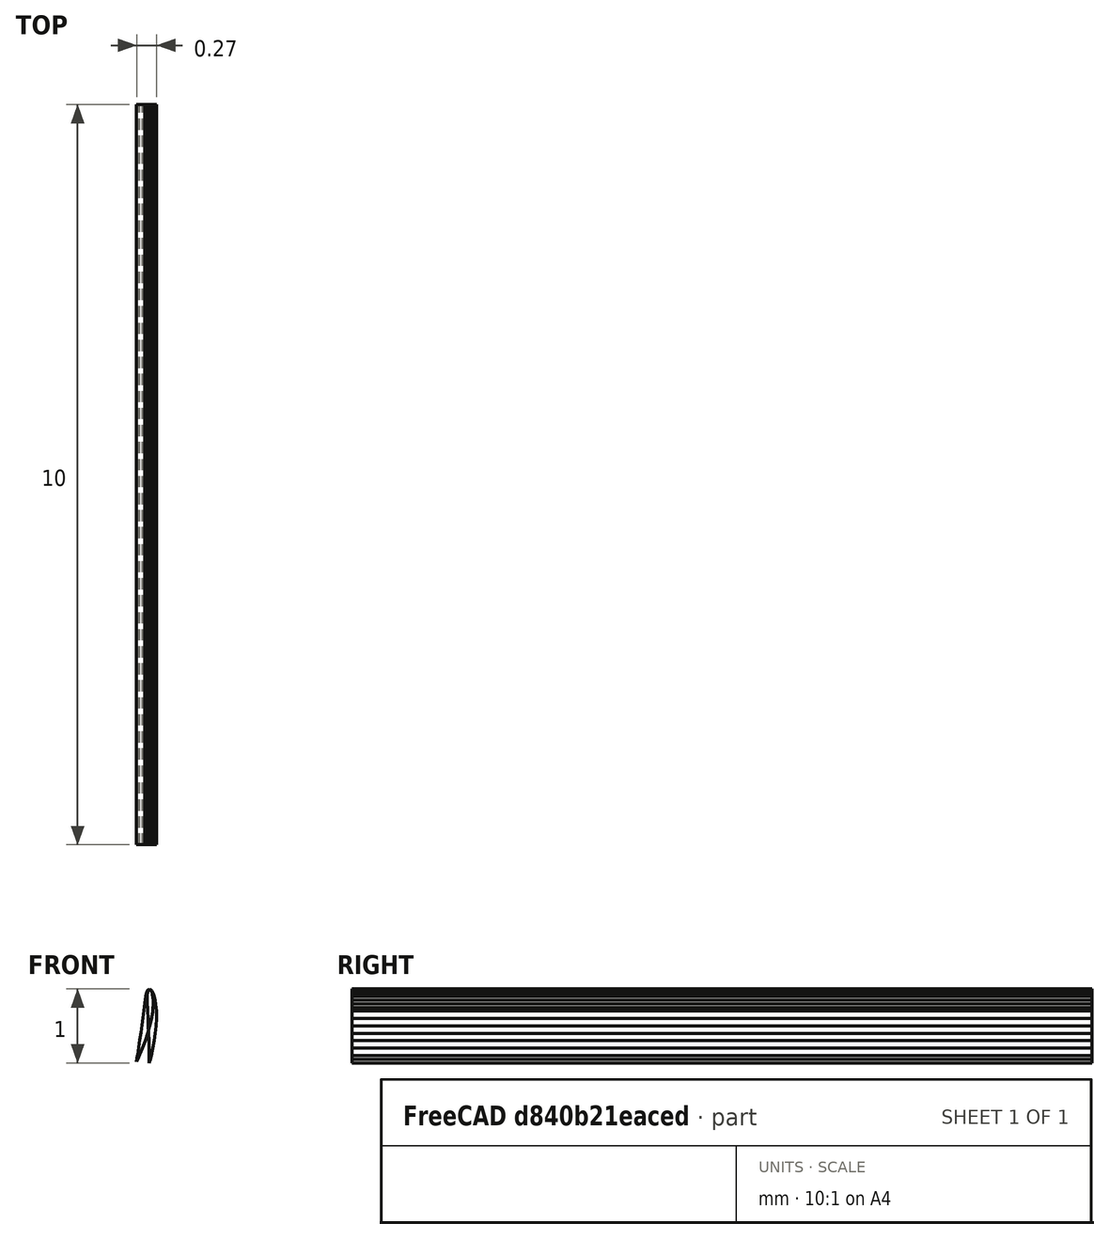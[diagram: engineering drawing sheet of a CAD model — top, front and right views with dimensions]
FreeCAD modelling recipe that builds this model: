
FCSTD DOCUMENT  (FreeCAD 0.20R29410 (Git))
Label: cavitating_hydrofoil
License: All rights reserved
LicenseURL: http://en.wikipedia.org/wiki/All_rights_reserved
objects: Part::Extrusion×2, Part::Part2DObjectPython×1, Sketcher::SketchObject×1, Part::Face×1
note: 5 computed .brp shape members not serialized (recipe doc carries the construction recipe); baked Part::Feature solids carry a one-line shape summary decoded from their .brp

FEATURE [Part::Part2DObjectPython] Wire  # Draft 2D object (typed FeaturePython)
  Area = 0.0820463
  ChamferSize = 0
  Closed = true
  End = (-0.0013,0,-1)
  FilletRadius = 0
  Length = 2.04636
  MakeFace = true
  Placement = pos=(0,0,0) rot=(0.57735,0.57735,-0.57735;2.0944rad)
  Points = (34) [(0.95,0.0147,0),(0.9,0.0271,0),(0.8,0.0489,0),(0.7,0.0669,0),(0.6,0.0814,0),(0.5,0.0919,0),(0.4,0.098,0),(0.3,0.0976,0),(0.25,0.0941,0),(0.2,0.088,0),+24 more]
  Start = (0.0147,0,-0.95)
  Subdivisions = 0
FEATURE [Sketcher::SketchObject] Sketch001
  FullyConstrained = false
  Placement = pos=(0,0,0) rot=(-1,0,0;1.5708rad)
  sketch-geometry (34):
    g0: LineSegment StartX=0.0147 StartY=0.95 StartZ=0 EndX=0.0271 EndY=0.9 EndZ=0
    g1: LineSegment StartX=0.0271 StartY=0.9 StartZ=0 EndX=0.0489 EndY=0.8 EndZ=0
    g2: LineSegment StartX=0.0489 StartY=0.8 StartZ=0 EndX=0.0669 EndY=0.7 EndZ=0
    g3: LineSegment StartX=0.0669 StartY=0.7 StartZ=0 EndX=0.0814 EndY=0.6 EndZ=0
    g4: LineSegment StartX=0.0814 StartY=0.6 StartZ=0 EndX=0.0919 EndY=0.5 EndZ=0
    g5: LineSegment StartX=0.0919 StartY=0.5 StartZ=0 EndX=0.098 EndY=0.4 EndZ=0
    g6: LineSegment StartX=0.098 StartY=0.4 StartZ=0 EndX=0.0976 EndY=0.3 EndZ=0
    g7: LineSegment StartX=0.0976 StartY=0.3 StartZ=0 EndX=0.0941 EndY=0.25 EndZ=0
    g8: LineSegment StartX=0.0941 StartY=0.25 StartZ=0 EndX=0.088 EndY=0.2 EndZ=0
    g9: LineSegment StartX=0.088 StartY=0.2 StartZ=0 EndX=0.0789 EndY=0.15 EndZ=0
    g10: LineSegment StartX=0.0789 StartY=0.15 StartZ=0 EndX=0.0659 EndY=0.1 EndZ=0
    g11: LineSegment StartX=0.0659 StartY=0.1 StartZ=0 EndX=0.0576 EndY=0.075 EndZ=0
    g12: LineSegment StartX=0.0576 StartY=0.075 StartZ=0 EndX=0.0473 EndY=0.05 EndZ=0
    g13: LineSegment StartX=0.0473 StartY=0.05 StartZ=0 EndX=0.0339 EndY=0.025 EndZ=0
    g14: LineSegment StartX=0.0339 StartY=0.025 StartZ=0 EndX=0.0244 EndY=0.0125 EndZ=0
    g15: LineSegment StartX=0.0244 StartY=0.0125 StartZ=0 EndX=0 EndY=0 EndZ=0
    g16: LineSegment StartX=0 StartY=0 StartZ=0 EndX=-0.0143 EndY=0.0125 EndZ=0
    g17: LineSegment StartX=-0.0143 StartY=0.0125 StartZ=0 EndX=-0.0195 EndY=0.025 EndZ=0
    g18: LineSegment StartX=-0.0195 StartY=0.025 StartZ=0 EndX=-0.0249 EndY=0.05 EndZ=0
    g19: LineSegment StartX=-0.0249 StartY=0.05 StartZ=0 EndX=-0.0274 EndY=0.075 EndZ=0
    g20: LineSegment StartX=-0.0274 StartY=0.075 StartZ=0 EndX=-0.0286 EndY=0.1 EndZ=0
    g21: LineSegment StartX=-0.0286 StartY=0.1 StartZ=0 EndX=-0.0288 EndY=0.15 EndZ=0
    g22: LineSegment StartX=-0.0288 StartY=0.15 StartZ=0 EndX=-0.0274 EndY=0.2 EndZ=0
    g23: LineSegment StartX=-0.0274 StartY=0.2 StartZ=0 EndX=-0.025 EndY=0.25 EndZ=0
    g24: LineSegment StartX=-0.025 StartY=0.25 StartZ=0 EndX=-0.0226 EndY=0.3 EndZ=0
    g25: LineSegment StartX=-0.0226 StartY=0.3 StartZ=0 EndX=-0.018 EndY=0.4 EndZ=0
    g26: LineSegment StartX=-0.018 StartY=0.4 StartZ=0 EndX=-0.014 EndY=0.5 EndZ=0
    g27: LineSegment StartX=-0.014 StartY=0.5 StartZ=0 EndX=-0.01 EndY=0.6 EndZ=0
    g28: LineSegment StartX=-0.01 StartY=0.6 StartZ=0 EndX=-0.0065 EndY=0.7 EndZ=0
    g29: LineSegment StartX=-0.0065 StartY=0.7 StartZ=0 EndX=-0.0039 EndY=0.8 EndZ=0
    g30: LineSegment StartX=-0.0039 StartY=0.8 StartZ=0 EndX=-0.0022 EndY=0.9 EndZ=0
    g31: LineSegment StartX=-0.0022 StartY=0.9 StartZ=0 EndX=-0.0016 EndY=0.95 EndZ=0
    g32: LineSegment StartX=-0.0016 StartY=0.95 StartZ=0 EndX=-0.0013 EndY=1 EndZ=0
    g33: LineSegment StartX=-0.0013 StartY=1 StartZ=0 EndX=0.0147 EndY=0.95 EndZ=0
  constraints (34):
    c: Coincident(g0,g1)
    c: Coincident(g1,g2)
    c: Coincident(g2,g3)
    c: Coincident(g3,g4)
    c: Coincident(g4,g5)
    c: Coincident(g5,g6)
    c: Coincident(g6,g7)
    c: Coincident(g7,g8)
    c: Coincident(g8,g9)
    c: Coincident(g9,g10)
    c: Coincident(g10,g11)
    c: Coincident(g11,g12)
    c: Coincident(g12,g13)
    c: Coincident(g13,g14)
    c: Coincident(g14,g15)
    c: Coincident(g15,g16)
    c: Coincident(g16,g17)
    c: Coincident(g17,g18)
    c: Coincident(g18,g19)
    c: Coincident(g19,g20)
    c: Coincident(g20,g21)
    c: Coincident(g21,g22)
    c: Coincident(g22,g23)
    c: Coincident(g23,g24)
    c: Coincident(g24,g25)
    c: Coincident(g25,g26)
    c: Coincident(g26,g27)
    c: Coincident(g27,g28)
    c: Coincident(g28,g29)
    c: Coincident(g29,g30)
    c: Coincident(g30,g31)
    c: Coincident(g31,g32)
    c: Coincident(g32,g33)
    c: Coincident(g33,g0)
FEATURE [Part::Face] Face
  FaceMakerClass = Part::FaceMakerBullseye
  Sources = -> [Sketch001]
FEATURE [Part::Extrusion] Extrude
  Base = -> Face
  Dir = (0,1,0)
  DirMode = 0
  FaceMakerClass = Part::FaceMakerBullseye
  LengthFwd = 10
  LengthRev = 0
  Solid = true
  Symmetric = true
FEATURE [Part::Extrusion] Extrude001
  Base = -> Face
  Dir = (0,1,0)
  DirMode = 0
  FaceMakerClass = Part::FaceMakerBullseye
  LengthFwd = 10
  LengthRev = 0
  Placement = pos=(0,0,0) rot=(0,1,0;0.174533rad)
  Solid = true
  Symmetric = true
